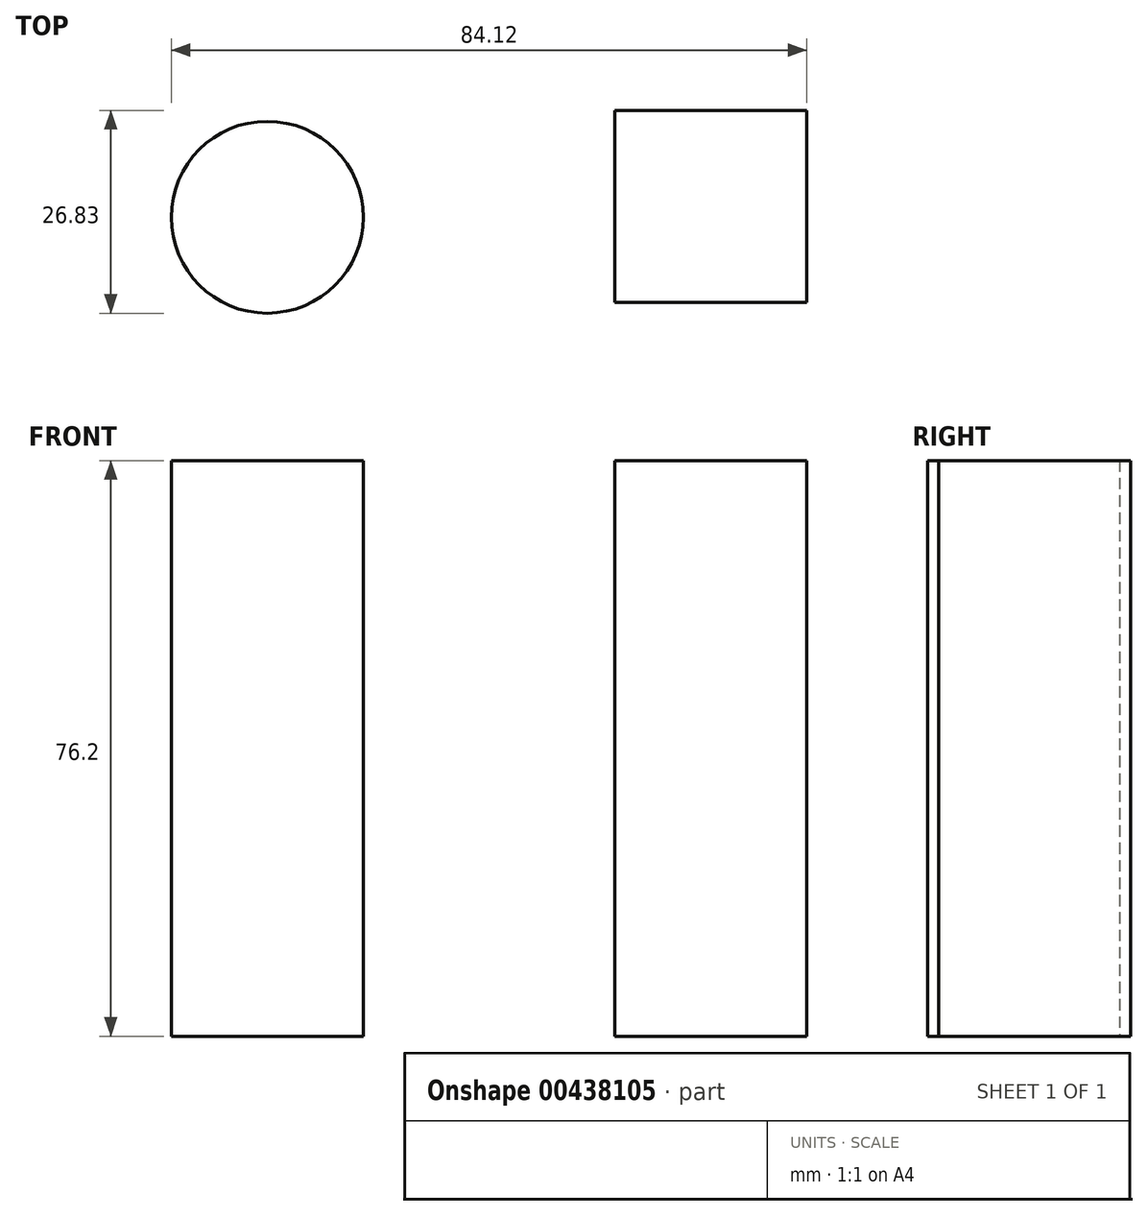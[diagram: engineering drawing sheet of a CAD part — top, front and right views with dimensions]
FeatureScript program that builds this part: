
annotation { "Feature Type Name" : "Feature", "Feature Type Description" : "" }
export const myFeature = defineFeature(function(context is Context, id is Id, definition is map)
    precondition{}
    {
        {
            var Q0;
            Q0=qCreatedBy(makeId("Top.planeOp"),FACE);
            var sketch = newSketch(context, id + "F0", { "sketchPlane" : qUnion([Q0])});
            skCircle(sketch, "E0", {"center": v(-29.03, 0) * mm, "radius": 12.7 * mm});
            skLineSegment(sketch, "E1.bottom", {"start": v(42.4, -11.27) * mm, "end": v(17, -11.27) * mm});
            skLineSegment(sketch, "E1.top", {"start": v(42.4, 14.13) * mm, "end": v(17, 14.13) * mm});
            skLineSegment(sketch, "E1.left", {"start": v(42.4, -11.27) * mm, "end": v(42.4, 14.13) * mm});
            skLineSegment(sketch, "E1.right", {"start": v(17, -11.27) * mm, "end": v(17, 14.13) * mm});
            skSolve(sketch);
        }
        {
            var Q0;
            Q0=makeQuery(id+"F0.imprint","IMPRINT",FACE,{"disambiguationData":[TD([[makeQuery(id+"F0.imprint","IMPRINT",EDGE,{"derivedFrom":sQuery(id+"F0.wireOp",EDGE,"E0")}),1.0]])]});
            var Q1;
            Q1=makeQuery(id+"F0.imprint","IMPRINT",FACE,{"disambiguationData":[TD([[makeQuery(id+"F0.imprint","IMPRINT",EDGE,{"derivedFrom":sQuery(id+"F0.wireOp",EDGE,"E1.bottom")}),-1.0]])]});
            extrude(context, id + "F1", {"entities" : qUnion([Q0, Q1]), "depth" : 76.2 * mm});
        }
    });
